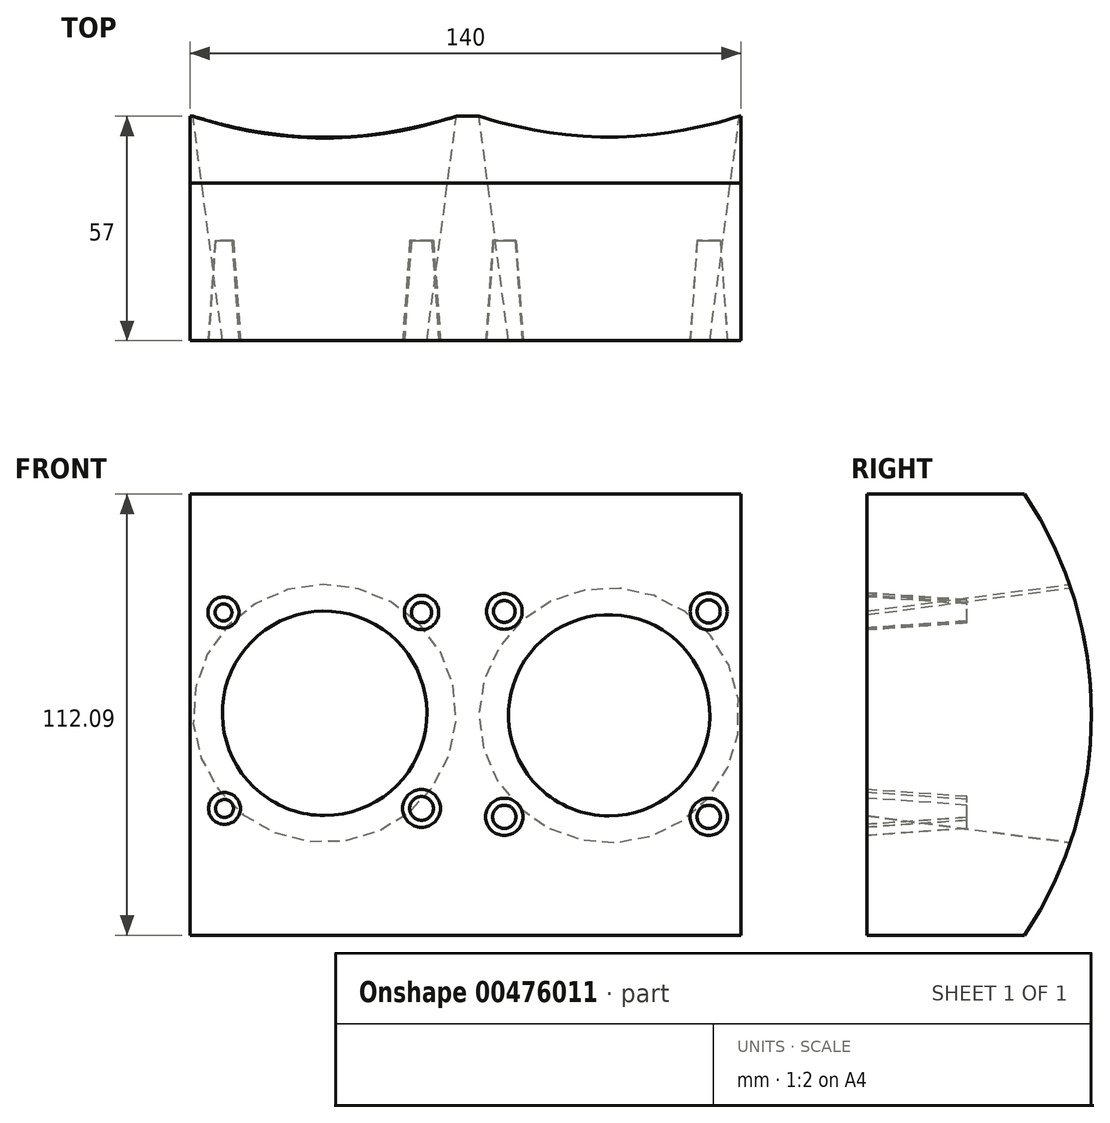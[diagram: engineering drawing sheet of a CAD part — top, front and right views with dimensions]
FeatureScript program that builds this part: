
annotation { "Feature Type Name" : "Feature", "Feature Type Description" : "" }
export const myFeature = defineFeature(function(context is Context, id is Id, definition is map)
    precondition{}
    {
        {
            var Q0;
            Q0=qCreatedBy(makeId("Right.planeOp"),FACE);
            var sketch = newSketch(context, id + "F0", { "sketchPlane" : qUnion([Q0])});
            skArc(sketch, "E0", {"start": v(0, -55.78) * mm, "mid": v(17, 0.27) * mm, "end": v(0, 56.31) * mm});
            skLineSegment(sketch, "E1", {"start": v(0, 56.31) * mm, "end": v(0, -55.78) * mm});
            skSolve(sketch);
        }
        {
            var Q0;
            Q0=makeQuery(id+"F0.imprint","IMPRINT",FACE,{"disambiguationData":[TD([[makeQuery(id+"F0.imprint","IMPRINT",EDGE,{"derivedFrom":sQuery(id+"F0.wireOp",EDGE,"E0")}),1.0]])]});
            extrude(context, id + "F1", {"entities" : qUnion([Q0]), "depth" : 70 * mm});
        }
        {
            var Q0;
            Q0=makeQuery(id+"F1.opExtrude","CAP_FACE",FACE,{"disambiguationData":[OSD([sQuery(id+"F0.wireOp",EDGE,"E0"),sQuery(id+"F0.wireOp",EDGE,"E1")])],"isStart":true});
            extrude(context, id + "F2", {"entities" : qUnion([Q0]), "operationType" : NewBodyOperationType.ADD, "depth" : 70 * mm});
        }
        {
            var Q0;
            {var subQ0=sQuery(id+"F0.wireOp",EDGE,"E1");Q0=makeQuery(id+"F2.boolean.opBoolean","MERGE",FACE,{"derivedFrom":[makeQuery(id+"F1.opExtrude","SWEPT_FACE",FACE,{"disambiguationData":[OSD([subQ0])]}),makeQuery(id+"F2.opExtrude","SWEPT_FACE",FACE,{"disambiguationData":[OSD([subQ0])]})]});}
            extrude(context, id + "F3", {"entities" : qUnion([Q0]), "operationType" : NewBodyOperationType.ADD, "depth" : 40 * mm});
        }
        {
            var Q0;
            Q0=makeQuery(id+"F3.opExtrude","CAP_FACE",FACE,{"disambiguationData":[OSD([sQuery(id+"F0.wireOp",EDGE,"E1")])],"isStart":false});
            var sketch = newSketch(context, id + "F4", { "sketchPlane" : qUnion([Q0])});
            skCircle(sketch, "E2", {"center": v(-35.81, 0.62) * mm, "radius": 25.97 * mm});
            skPoint(sketch, "E2.first.point", {"position": v(-9.85, 0) * mm});
            skPoint(sketch, "E2.second.point", {"position": v(-61.77, 0) * mm});
            skPoint(sketch, "E2.third.point", {"position": v(-49.52, -21.43) * mm});
            skCircle(sketch, "E3", {"center": v(36.48, 0.1) * mm, "radius": 25.56 * mm});
            skPoint(sketch, "E3.first.point", {"position": v(10.92, 0) * mm});
            skPoint(sketch, "E3.second.point", {"position": v(62.04, 0.62) * mm});
            skPoint(sketch, "E3.third.point", {"position": v(61.24, -6.26) * mm});
            skSolve(sketch);
        }
        {
            var Q0;
            Q0 = qSketchRegion(id + "F4", true);
            extrude(context, id + "F5", {"entities" : qUnion([Q0]), "operationType" : NewBodyOperationType.REMOVE, "oppositeDirection" : true, "depth" : 101.6 * mm, "hasDraft" : true, "draftAngle" : 7.5 * degree});
        }
        {
            var Q0;
            Q0=makeQuery(id+"F3.opExtrude","CAP_FACE",FACE,{"disambiguationData":[OSD([sQuery(id+"F0.wireOp",EDGE,"E1")])],"isStart":false});
            var sketch = newSketch(context, id + "F6", { "sketchPlane" : qUnion([Q0])});
            skCircle(sketch, "E4", {"center": v(-61.5, 26.23) * mm, "radius": 3.93 * mm});
            skCircle(sketch, "E5", {"center": v(-11.18, 26.23) * mm, "radius": 4.37 * mm});
            skSolve(sketch);
        }
        {
            var Q0;
            Q0=makeQuery(id+"F6.imprint","IMPRINT",FACE,{"disambiguationData":[TD([[makeQuery(id+"F6.imprint","IMPRINT",EDGE,{"derivedFrom":sQuery(id+"F6.wireOp",EDGE,"E4")}),-1.0]])]});
            var sketch = newSketch(context, id + "F7", { "sketchPlane" : qUnion([Q0])});
            skCircle(sketch, "E6", {"center": v(-61.24, -23.56) * mm, "radius": 4.06 * mm});
            skCircle(sketch, "E7", {"center": v(-11.18, -23.56) * mm, "radius": 4.8 * mm});
            skSolve(sketch);
        }
        {
            var Q0;
            Q0=makeQuery(id+"F6.imprint","IMPRINT",FACE,{"disambiguationData":[TD([[makeQuery(id+"F6.imprint","IMPRINT",EDGE,{"derivedFrom":sQuery(id+"F6.wireOp",EDGE,"E4")}),1.0]])]});
            var Q1;
            Q1=makeQuery(id+"F6.imprint","IMPRINT",FACE,{"disambiguationData":[TD([[makeQuery(id+"F6.imprint","IMPRINT",EDGE,{"derivedFrom":sQuery(id+"F6.wireOp",EDGE,"E5")}),1.0]])]});
            var Q2;
            Q2=makeQuery(id+"F7.imprint","IMPRINT",FACE,{"disambiguationData":[TD([[makeQuery(id+"F7.imprint","IMPRINT",EDGE,{"derivedFrom":sQuery(id+"F7.wireOp",EDGE,"E6")}),1.0]])]});
            var Q3;
            Q3=makeQuery(id+"F7.imprint","IMPRINT",FACE,{"disambiguationData":[TD([[makeQuery(id+"F7.imprint","IMPRINT",EDGE,{"derivedFrom":sQuery(id+"F7.wireOp",EDGE,"E7")}),1.0]])]});
            var Q4;
            Q4=sQuery(id+"F6.wireOp",EDGE,"E5");
            var Q5;
            Q5=sQuery(id+"F6.wireOp",EDGE,"E4");
            var Q6;
            Q6=sQuery(id+"F7.wireOp",EDGE,"E6");
            var Q7;
            Q7=sQuery(id+"F7.wireOp",EDGE,"E7");
            extrude(context, id + "F8", {"entities" : qUnion([Q0, Q1, Q2, Q3]), "operationType" : NewBodyOperationType.REMOVE, "surfaceEntities" : qUnion([Q4, Q5, Q6, Q7]), "oppositeDirection" : true, "depth" : 25.4 * mm, "hasDraft" : true, "draftAngle" : 4 * degree, "draftPullDirection" : true});
        }
        {
            var Q0;
            Q0=makeQuery(id+"F3.opExtrude","CAP_FACE",FACE,{"disambiguationData":[OSD([sQuery(id+"F0.wireOp",EDGE,"E1")])],"isStart":false});
            var sketch = newSketch(context, id + "F9", { "sketchPlane" : qUnion([Q0])});
            skCircle(sketch, "E8", {"center": v(9.85, 26.5) * mm, "radius": 4.53 * mm});
            skCircle(sketch, "E9", {"center": v(61.77, 26.5) * mm, "radius": 4.71 * mm});
            skCircle(sketch, "E10", {"center": v(61.77, -25.7) * mm, "radius": 4.74 * mm});
            skCircle(sketch, "E11", {"center": v(9.85, -25.7) * mm, "radius": 4.74 * mm});
            skSolve(sketch);
        }
        {
            var Q0;
            Q0=makeQuery(id+"F9.imprint","IMPRINT",FACE,{"disambiguationData":[TD([[makeQuery(id+"F9.imprint","IMPRINT",EDGE,{"derivedFrom":sQuery(id+"F9.wireOp",EDGE,"E8")}),1.0]])]});
            var Q1;
            Q1=makeQuery(id+"F9.imprint","IMPRINT",FACE,{"disambiguationData":[TD([[makeQuery(id+"F9.imprint","IMPRINT",EDGE,{"derivedFrom":sQuery(id+"F9.wireOp",EDGE,"E9")}),1.0]])]});
            var Q2;
            Q2=makeQuery(id+"F9.imprint","IMPRINT",FACE,{"disambiguationData":[TD([[makeQuery(id+"F9.imprint","IMPRINT",EDGE,{"derivedFrom":sQuery(id+"F9.wireOp",EDGE,"E10")}),1.0]])]});
            var Q3;
            Q3=makeQuery(id+"F9.imprint","IMPRINT",FACE,{"disambiguationData":[TD([[makeQuery(id+"F9.imprint","IMPRINT",EDGE,{"derivedFrom":sQuery(id+"F9.wireOp",EDGE,"E11")}),1.0]])]});
            var Q4;
            Q4=sQuery(id+"F9.wireOp",EDGE,"E8");
            var Q5;
            Q5=sQuery(id+"F9.wireOp",EDGE,"E9");
            var Q6;
            Q6=sQuery(id+"F9.wireOp",EDGE,"E10");
            var Q7;
            Q7=sQuery(id+"F9.wireOp",EDGE,"E11");
            extrude(context, id + "F10", {"entities" : qUnion([Q0, Q1, Q2, Q3]), "operationType" : NewBodyOperationType.REMOVE, "surfaceEntities" : qUnion([Q4, Q5, Q6, Q7]), "oppositeDirection" : true, "depth" : 25.4 * mm, "hasDraft" : true, "draftAngle" : 4 * degree, "draftPullDirection" : true});
        }
    });
